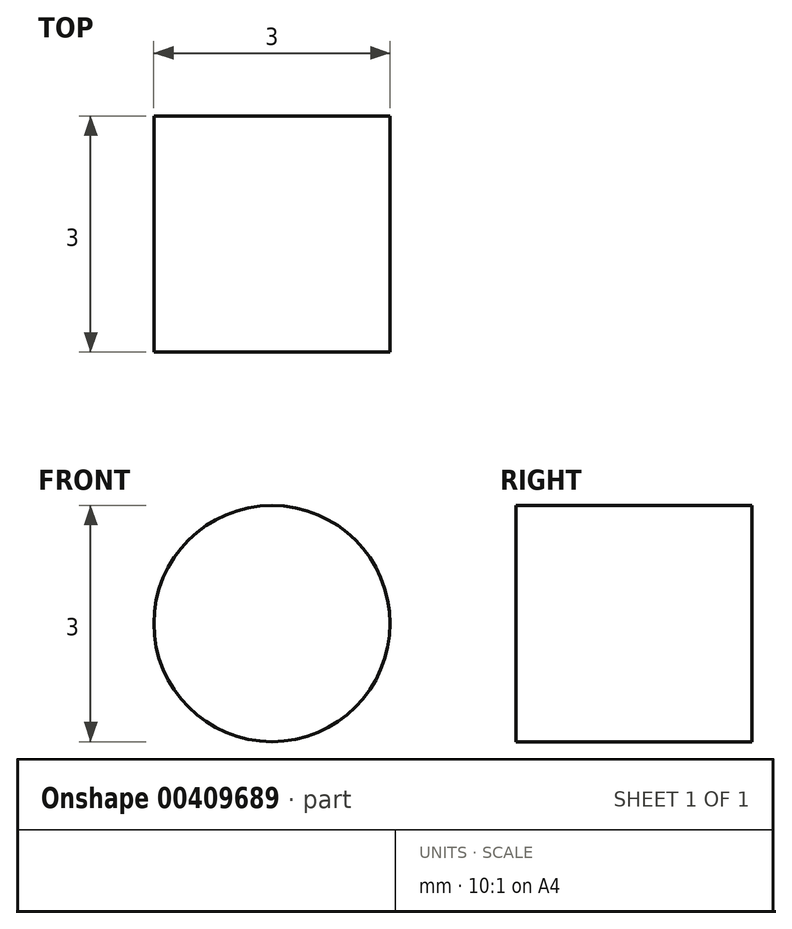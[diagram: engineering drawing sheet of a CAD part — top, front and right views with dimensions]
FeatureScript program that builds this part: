
annotation { "Feature Type Name" : "Feature", "Feature Type Description" : "" }
export const myFeature = defineFeature(function(context is Context, id is Id, definition is map)
    precondition{}
    {
        {
            var Q0;
            Q0=qCreatedBy(makeId("Front.planeOp"),FACE);
            var sketch = newSketch(context, id + "F0", { "sketchPlane" : qUnion([Q0])});
            skCircle(sketch, "E0", {"center": v(0, 0) * mm, "radius": 45 * mm, "construction": true});
            skLineSegment(sketch, "E1", {"start": v(0, 0) * mm, "end": v(-38.97, 22.5) * mm, "construction": true});
            skLineSegment(sketch, "E2.MirrorCS", {"start": v(0, 0) * mm, "end": v(38.97, 22.5) * mm, "construction": true});
            skLineSegment(sketch, "E3", {"start": v(0, 0) * mm, "end": v(0, -45) * mm, "construction": true});
            skPoint(sketch, "E4", {"position": v(-25.98, 15) * mm});
            skPoint(sketch, "E5.MirrorP", {"position": v(25.98, 15) * mm});
            skPoint(sketch, "E6", {"position": v(0, -30) * mm});
            skCircle(sketch, "E7", {"center": v(-34.64, 20) * mm, "radius": 5 * mm, "construction": true});
            skCircle(sketch, "E8", {"center": v(0, -40) * mm, "radius": 5 * mm, "construction": true});
            skLineSegment(sketch, "E9", {"start": v(-34.64, 20) * mm, "end": v(-38.97, 17.5) * mm, "construction": true});
            skLineSegment(sketch, "E10.MirrorCS", {"start": v(34.64, 20) * mm, "end": v(38.97, 17.5) * mm, "construction": true});
            skLineSegment(sketch, "E11", {"start": v(0, -40) * mm, "end": v(4.33, -42.5) * mm, "construction": true});
            skLineSegment(sketch, "E12", {"start": v(0, 0) * mm, "end": v(-38.97, -22.5) * mm, "construction": true});
            skLineSegment(sketch, "E13", {"start": v(0, 0) * mm, "end": v(38.97, -22.5) * mm, "construction": true});
            skPoint(sketch, "E14", {"position": v(-17.32, -10) * mm});
            skPoint(sketch, "E15.MirrorP", {"position": v(17.32, -10) * mm});
            skLineSegment(sketch, "E16.MirrorCS", {"start": v(0, -40) * mm, "end": v(-4.33, -42.5) * mm, "construction": true});
            skArc(sketch, "E17", {"start": v(-4.33, -42.5) * mm, "mid": v(-17.32, -10) * mm, "end": v(-38.97, 17.5) * mm});
            skArc(sketch, "E18.MirrorCS", {"start": v(4.33, -42.5) * mm, "mid": v(17.32, -10) * mm, "end": v(38.97, 17.5) * mm});
            skArc(sketch, "E19", {"start": v(-4.33, -42.5) * mm, "mid": v(0, -45) * mm, "end": v(4.33, -42.5) * mm});
            skLineSegment(sketch, "E20", {"start": v(0, 0) * mm, "end": v(0, 45) * mm, "construction": true});
            skPoint(sketch, "E21", {"position": v(0, 20) * mm});
            skLineSegment(sketch, "E22", {"start": v(-34.64, 20) * mm, "end": v(-34.64, 25) * mm, "construction": true});
            skCircle(sketch, "E23.MirrorC", {"center": v(34.64, 20) * mm, "radius": 5 * mm, "construction": true});
            skLineSegment(sketch, "E24.MirrorCS", {"start": v(34.64, 20) * mm, "end": v(34.64, 25) * mm, "construction": true});
            skArc(sketch, "E25", {"start": v(-34.64, 25) * mm, "mid": v(0, 20) * mm, "end": v(34.64, 25) * mm});
            skArc(sketch, "E26", {"start": v(38.97, 17.5) * mm, "mid": v(38.97, 22.5) * mm, "end": v(34.64, 25) * mm});
            skArc(sketch, "E27", {"start": v(-34.64, 25) * mm, "mid": v(-38.97, 22.5) * mm, "end": v(-38.97, 17.5) * mm});
            skSolve(sketch);
        }
        {
            var Q0;
            Q0=makeQuery(id+"F0.imprint","IMPRINT",FACE,{"disambiguationData":[TD([[makeQuery(id+"F0.imprint","IMPRINT",EDGE,{"derivedFrom":sQuery(id+"F0.wireOp",EDGE,"E17")}),-1.0]])]});
            extrude(context, id + "F1", {"entities" : qUnion([Q0]), "depth" : 3 * mm});
        }
        {
            var Q0;
            Q0=makeQuery(id+"F1.opExtrude","CAP_FACE",FACE,{"disambiguationData":[OSD([sQuery(id+"F0.wireOp",EDGE,"E17"),sQuery(id+"F0.wireOp",EDGE,"E18.MirrorCS"),sQuery(id+"F0.wireOp",EDGE,"E19"),sQuery(id+"F0.wireOp",EDGE,"E25"),sQuery(id+"F0.wireOp",EDGE,"E26"),sQuery(id+"F0.wireOp",EDGE,"E27")])],"isStart":false});
            var sketch = newSketch(context, id + "F2", { "sketchPlane" : qUnion([Q0])});
            skLineSegment(sketch, "E28", {"start": v(0, 0) * mm, "end": v(-51.96, 30) * mm, "construction": true});
            skLineSegment(sketch, "E29", {"start": v(0, 0) * mm, "end": v(0, -58.48) * mm, "construction": true});
            skLineSegment(sketch, "E30.MirrorCS", {"start": v(0, 0) * mm, "end": v(51.96, 30) * mm, "construction": true});
            skPoint(sketch, "E31", {"position": v(-25.98, 15) * mm});
            skPoint(sketch, "E32.MirrorP", {"position": v(25.98, 15) * mm});
            skPoint(sketch, "E33", {"position": v(0, -30) * mm});
            skCircle(sketch, "E34", {"center": v(-25.98, 15) * mm, "radius": 1.5 * mm});
            skCircle(sketch, "E35", {"center": v(0, -30) * mm, "radius": 1.5 * mm});
            skCircle(sketch, "E36", {"center": v(0, 0) * mm, "radius": 14.5 * mm});
            skCircle(sketch, "E37.MirrorC", {"center": v(25.98, 15) * mm, "radius": 1.5 * mm});
            skSolve(sketch);
        }
        {
            var Q0;
            Q0=makeQuery(id+"F2.imprint","IMPRINT",FACE,{"disambiguationData":[TD([[makeQuery(id+"F2.imprint","IMPRINT",EDGE,{"derivedFrom":sQuery(id+"F2.wireOp",EDGE,"E34")}),1.0]])]});
            var Q1;
            Q1=makeQuery(id+"F2.imprint","IMPRINT",FACE,{"disambiguationData":[TD([[makeQuery(id+"F2.imprint","IMPRINT",EDGE,{"derivedFrom":sQuery(id+"F2.wireOp",EDGE,"E36")}),1.0]])]});
            var Q2;
            Q2=makeQuery(id+"F2.imprint","IMPRINT",FACE,{"disambiguationData":[TD([[makeQuery(id+"F2.imprint","IMPRINT",EDGE,{"derivedFrom":sQuery(id+"F2.wireOp",EDGE,"E37.MirrorC")}),-1.0]])]});
            var Q3;
            Q3=makeQuery(id+"F2.imprint","IMPRINT",FACE,{"disambiguationData":[TD([[makeQuery(id+"F2.imprint","IMPRINT",EDGE,{"derivedFrom":sQuery(id+"F2.wireOp",EDGE,"E35")}),1.0]])]});
            extrude(context, id + "F3", {"entities" : qUnion([Q0, Q1, Q2, Q3]), "operationType" : NewBodyOperationType.REMOVE, "endBound" : BoundingType.THROUGH_ALL, "oppositeDirection" : true, "depth" : 25 * mm});
        }
    });
